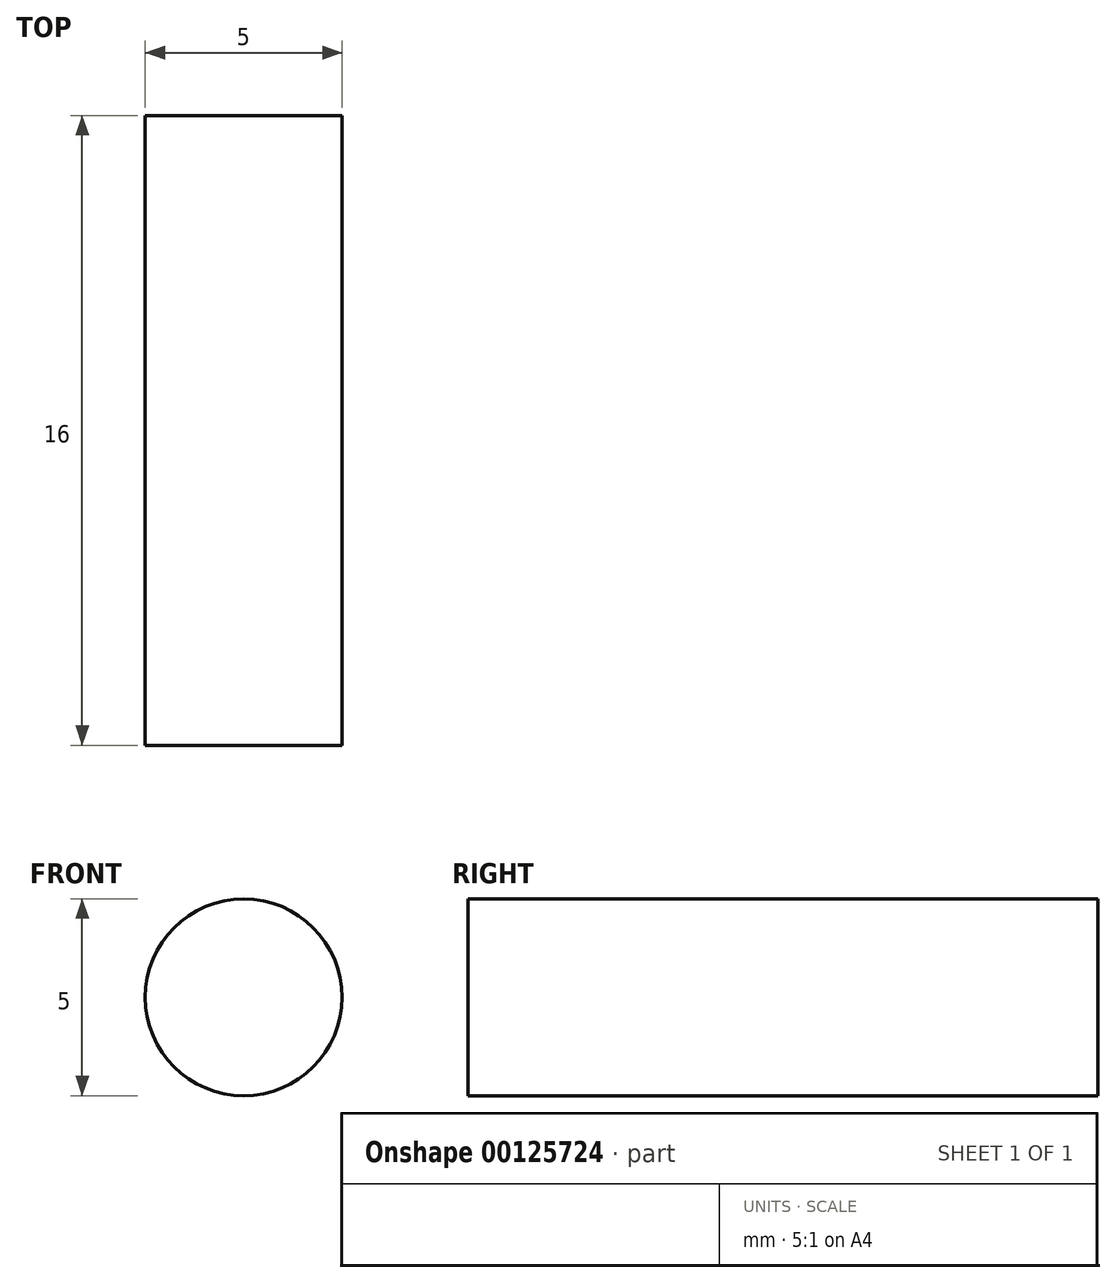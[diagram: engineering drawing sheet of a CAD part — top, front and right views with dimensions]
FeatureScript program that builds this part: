
annotation { "Feature Type Name" : "Feature", "Feature Type Description" : "" }
export const myFeature = defineFeature(function(context is Context, id is Id, definition is map)
    precondition{}
    {
        {
            var Q0;
            Q0=qCreatedBy(makeId("Front.planeOp"),FACE);
            var sketch = newSketch(context, id + "F0", { "sketchPlane" : qUnion([Q0])});
            skCircle(sketch, "E0", {"center": v(0, 0) * mm, "radius": 2.5 * mm});
            skSolve(sketch);
        }
        {
            var Q0;
            Q0 = qSketchRegion(id + "F0", true);
            extrude(context, id + "F1", {"entities" : qUnion([Q0]), "depth" : 16 * mm, "symmetric" : true});
        }
    });
